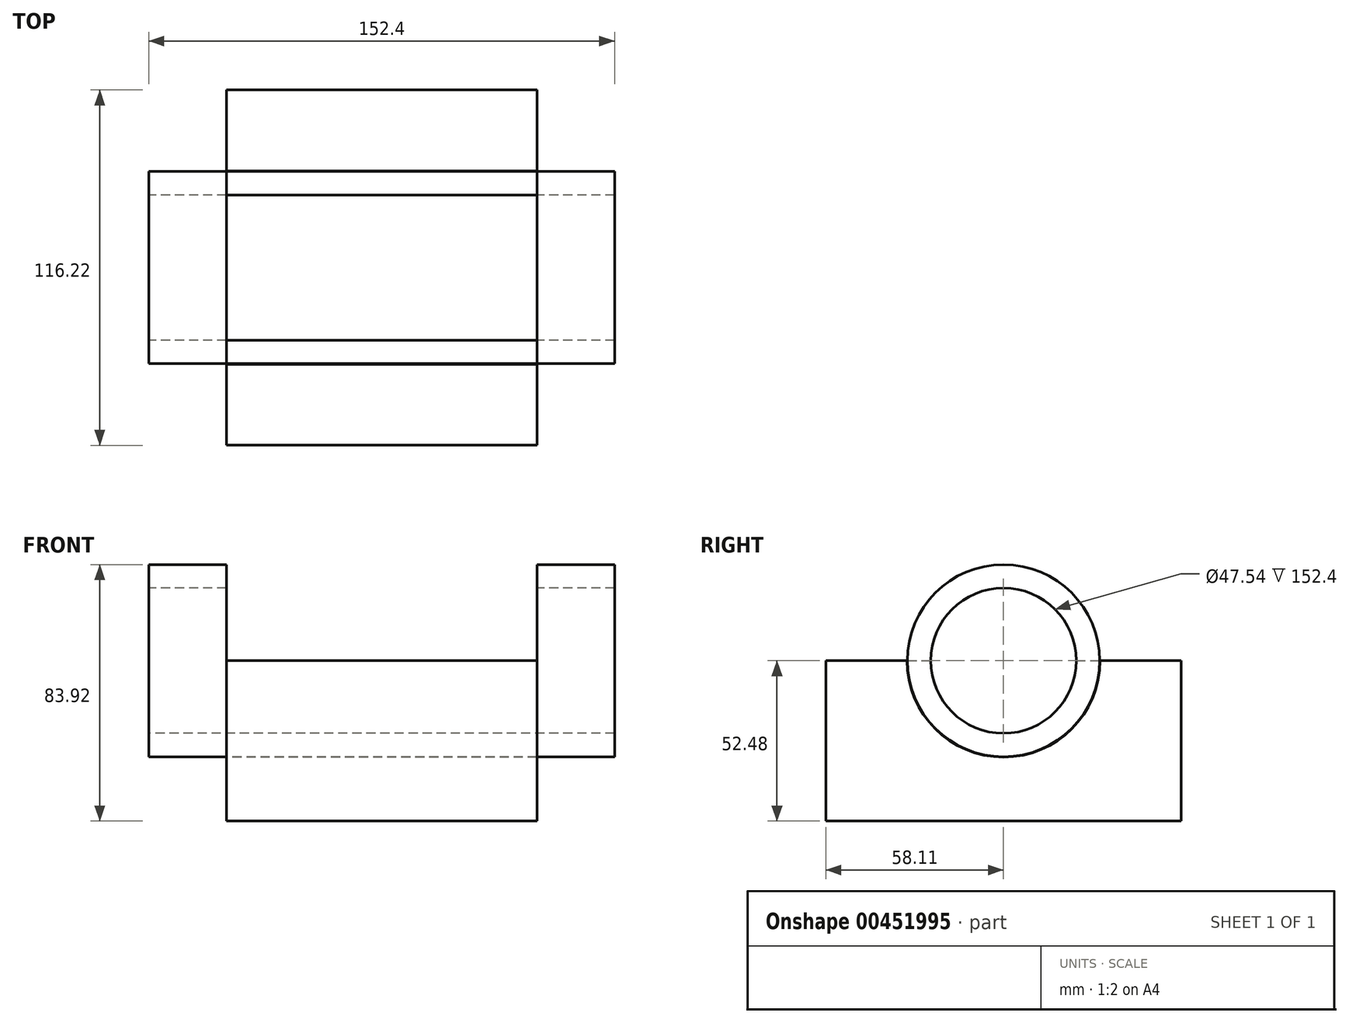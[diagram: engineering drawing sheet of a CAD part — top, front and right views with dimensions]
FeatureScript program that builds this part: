
annotation { "Feature Type Name" : "Feature", "Feature Type Description" : "" }
export const myFeature = defineFeature(function(context is Context, id is Id, definition is map)
    precondition{}
    {
        {
            var Q0;
            Q0=qCreatedBy(makeId("Right.planeOp"),FACE);
            var sketch = newSketch(context, id + "F0", { "sketchPlane" : qUnion([Q0])});
            skCircle(sketch, "E0", {"center": v(0, 0) * mm, "radius": 31.58 * mm});
            skLineSegment(sketch, "E1.bottom", {"start": v(58.1, -52.48) * mm, "end": v(-58.1, -52.48) * mm});
            skLineSegment(sketch, "E1.top", {"start": v(58.1, 52.48) * mm, "end": v(-58.1, 52.48) * mm});
            skLineSegment(sketch, "E1.left", {"start": v(58.1, -52.48) * mm, "end": v(58.1, 52.48) * mm});
            skLineSegment(sketch, "E1.right", {"start": v(-58.1, -52.48) * mm, "end": v(-58.1, 52.48) * mm});
            skSolve(sketch);
        }
        {
            var Q0;
            Q0 = qSketchRegion(id + "F0", true);
            extrude(context, id + "F1", {"entities" : qUnion([Q0]), "endBound" : BoundingType.SYMMETRIC, "depth" : 101.6 * mm});
        }
        {
            var Q0;
            Q0=qCreatedBy(makeId("Right.planeOp"),FACE);
            var sketch = newSketch(context, id + "F2", { "sketchPlane" : qUnion([Q0])});
            skCircle(sketch, "E2", {"center": v(0, 0) * mm, "radius": 31.44 * mm});
            skCircle(sketch, "E3", {"center": v(0, 0) * mm, "radius": 23.77 * mm});
            skSolve(sketch);
        }
        {
            var Q0;
            Q0 = qSketchRegion(id + "F2", true);
            extrude(context, id + "F3", {"entities" : qUnion([Q0]), "endBound" : BoundingType.SYMMETRIC, "depth" : 152.4 * mm});
        }
        {
            var Q0;
            Q0=qCreatedBy(makeId("Right.planeOp"),FACE);
            var sketch = newSketch(context, id + "F4", { "sketchPlane" : qUnion([Q0])});
            skLineSegment(sketch, "E4", {"start": v(-63.96, 0) * mm, "end": v(66.92, 0) * mm});
            skLineSegment(sketch, "E5", {"start": v(66.92, 0) * mm, "end": v(66.92, 69.14) * mm});
            skLineSegment(sketch, "E6", {"start": v(66.92, 69.14) * mm, "end": v(-65.69, 69.14) * mm});
            skLineSegment(sketch, "E7", {"start": v(-65.69, 69.14) * mm, "end": v(-63.96, 0) * mm});
            skSolve(sketch);
        }
        {
            var Q0;
            Q0 = qSketchRegion(id + "F4", true);
            extrude(context, id + "F5", {"entities" : qUnion([Q0]), "operationType" : NewBodyOperationType.REMOVE, "endBound" : BoundingType.SYMMETRIC, "depth" : 101.6 * mm});
        }
    });
